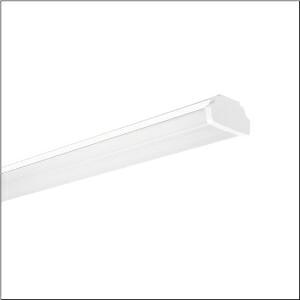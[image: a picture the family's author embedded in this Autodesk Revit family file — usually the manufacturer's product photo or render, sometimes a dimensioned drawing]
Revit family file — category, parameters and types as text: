
# Revit family: modario_r__31_mo_53bm81271v4080_0fb4
name_source: partatom
category: Lighting Fixtures
units: mm (PartAtom-declared; Revit-internal decimal feet)

## family parameters
Cut with Voids When Loaded = No
Host = Face
Light Source = No
Part Type = Normal
Room Calculation Point = No
Round Connector Dimension = Use Diameter
Shared = No

## types (1)
- Modario® 31 MO (1 x LED, 7810 lm, 50.8 W, 4000K)
    Apparent Load = 51 VA
    CIE Flux Codes = 47 80 95 92 100
    Color Rendering = 80
    Color Temperature = 4000K
    Default Elevation = 1800 mm
    Description = Modario® 31 MO, luminaire insert, of sheet steel, coil coated, white, length: 1.495mm, width: 81mm, height: 82mm, 5x system unit, system units: 299mm, LED rated luminous flux: 7.810lm, light colour: 840, control gear: ON/OFF, control gear: ECG, with plug, 3-pole, with phase selection, mains connection: 220..240V, AC, 50/60Hz, rated input power: 51W, through-wiring accessed according to module size, primary optical cover: cover, of PMMA, light emission: direct distribution, primary light characteristic: symmetric, protection rating (complete): IP20, protection rating (LED compartment): IP50, insulation class (complete): insulation class I (protective earthing), certification: CE, ENEC, VDE, UKCA, impact resistance: IK03, permissible ambient temperature for indoor applications: -35..+35°C, corresponds to IFS (International Featured Standards) requirements for safety and quality in the food industry, reducing of maximum allowable ambient temperature of 5°C with ceiling mounting, packaging unit: 1 piece
    Height = 92 mm
    Lamp = 1 x LED
    Lamp Light Flux = 7810 lm
    Lamp Power = 50.8 W
    Lamp count = 1
    Length = 1495 mm
    Luminous efficacy = 154 lm/W
    Manufacturer = Siteco
    ModVariant = No
    Model = 53BM81271V4080
    Mounting Place = Ceiling
    Mounting Type = Pendant
    Number of Poles = 1
    OnlyDefault = Yes
    Power Factor = 1
    Product Name = Modario® 31 MO
    Product group = luminaire insert
    ProductGroupID = 901
    Protection Class = Protection class I
    Protection Degree = IP 20
    RLX_Detail_Level = 1
    RLX_Emergency_Light_Flux = 0 lm
    RLX_Emergency_Type = 0
    RLX_Emergency_Type_DB = No
    RlxData = <blob elided: 38681 chars, md5=f7437e05>
    Socket = socket
    Standby Power = 0 W
    System Light Flux = 7810 lm
    System Power = 51 W
    Type Comments = Product without accessories
    Type Image = l_1300283.jpg
    URL = http://relux.com
    VarID = ---
    Voltage = 0 V
    Weight = 0.00 kg
    Width = 81 mm

## geometry (parser evidence)
native form markers: Blend x4, Sweep x12
no freeform markers — native parametric forms only
